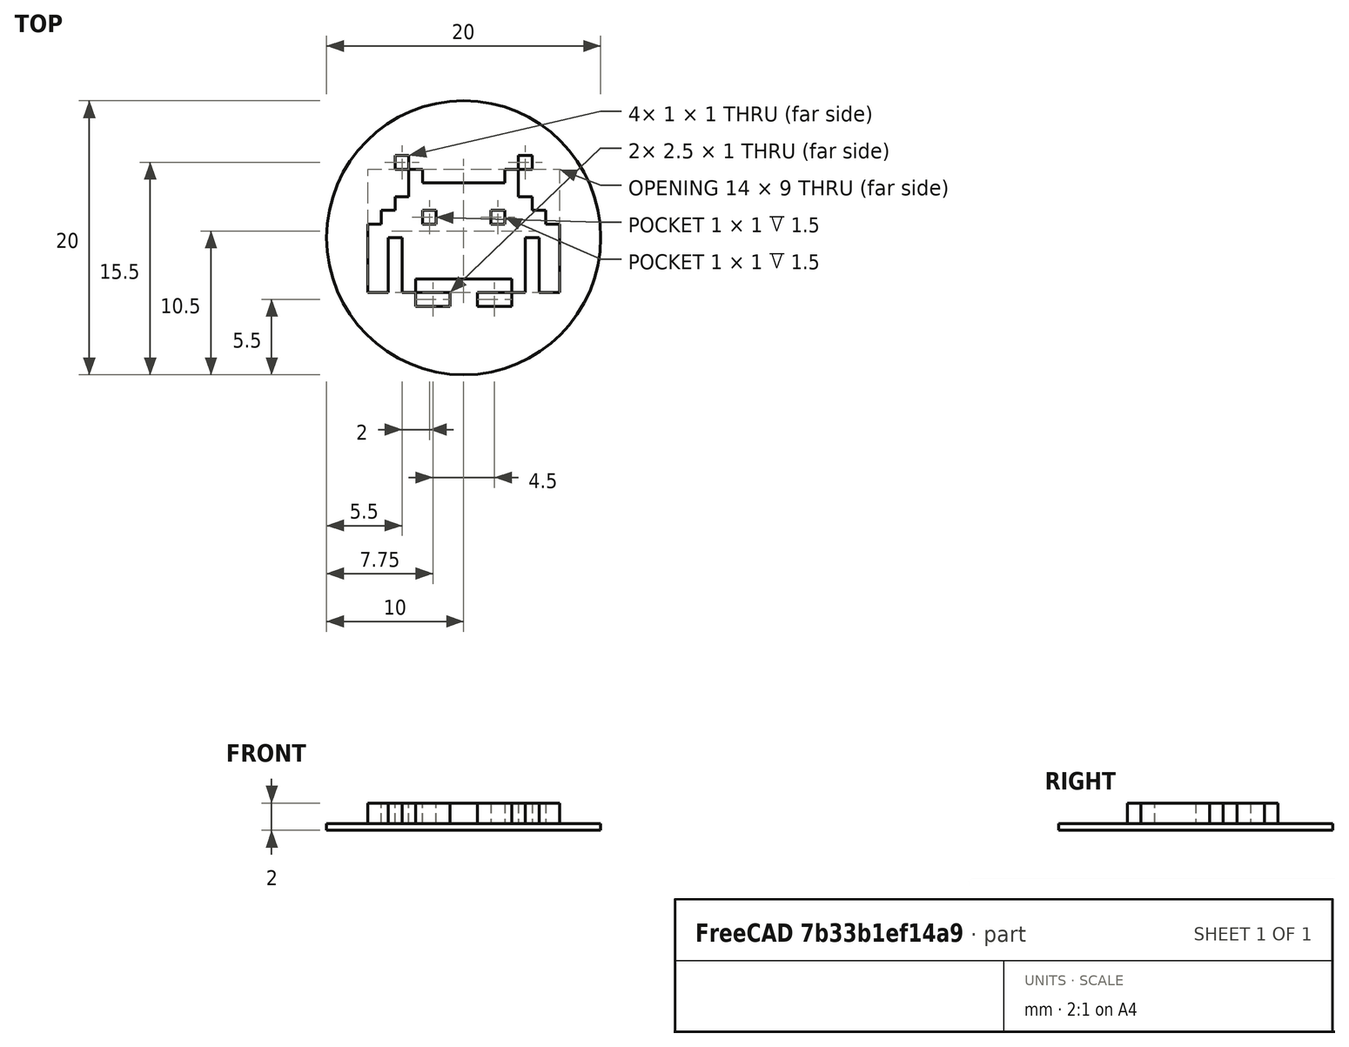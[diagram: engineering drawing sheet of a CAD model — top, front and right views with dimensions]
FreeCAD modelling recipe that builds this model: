
FCSTD DOCUMENT  (FreeCAD 0.20R29177 +233 (Git))
Label: marcianito
License: All rights reserved
LicenseURL: http://en.wikipedia.org/wiki/All_rights_reserved
objects: Part::Box×30, Part::Cut×22, Part::MultiFuse×4, Part::Cylinder×1
note: 57 computed .brp shape members not serialized (recipe doc carries the construction recipe); baked Part::Feature solids carry a one-line shape summary decoded from their .brp

FEATURE [Part::Cylinder] Cylinder  label="Cilindro"
  Angle = 360
  AttacherType = Attacher::AttachEngine3D
  FirstAngle = 0
  Height = 0.5
  Radius = 10
  SecondAngle = 0
FEATURE [Part::Box] Box  label="Cubo"
  AttacherType = Attacher::AttachEngine3D
  Height = 2
  Length = 7
  Placement = pos=(-7,-5,0) rot=(0,0,1;0rad)
  Width = 10
FEATURE [Part::Box] Box001  label="Cubo001"
  AttacherType = Attacher::AttachEngine3D
  Height = 2
  Length = 1
  Placement = pos=(-7,0,0) rot=(0,0,1;0rad)
  Width = 1
FEATURE [Part::Box] Box002  label="Cubo002"
  AttacherType = Attacher::AttachEngine3D
  Height = 2
  Length = 1
  Placement = pos=(-3,0,0) rot=(0,0,1;0rad)
  Width = 1
FEATURE [Part::Box] Box003  label="Cubo003"
  AttacherType = Attacher::AttachEngine3D
  Height = 2
  Length = 1
  Placement = pos=(-5,2,0) rot=(0,0,1;0rad)
  Width = 1
FEATURE [Part::Box] Box004  label="Cubo004"
  AttacherType = Attacher::AttachEngine3D
  Height = 2
  Length = 4
  Placement = pos=(-5.5,-1,0) rot=(0,0,1;4.71239rad)
  Width = 1
FEATURE [Part::Box] Box005  label="Cubo005"
  AttacherType = Attacher::AttachEngine3D
  Height = 2
  Length = 1
  Placement = pos=(-5,4,0) rot=(0,0,1;0rad)
  Width = 1
FEATURE [Part::Box] Box006  label="Cubo006"
  AttacherType = Attacher::AttachEngine3D
  Height = 2
  Length = 1
  Placement = pos=(-6,1,0) rot=(0,0,1;0rad)
  Width = 1
FEATURE [Part::Box] Box007  label="Cubo007"
  AttacherType = Attacher::AttachEngine3D
  Height = 2
  Length = 4
  Placement = pos=(-4,3,0) rot=(0,0,1;0rad)
  Width = 1
FEATURE [Part::Box] Box008  label="Cubo008"
  AttacherType = Attacher::AttachEngine3D
  Height = 2
  Length = 3.5
  Placement = pos=(-3.5,-5,0) rot=(0,0,1;0rad)
  Width = 1
FEATURE [Part::Cut] Cut
  Base = -> Box
  Tool = -> Box001
FEATURE [Part::Cut] Cut001
  Base = -> Cut
  Tool = -> Box008
FEATURE [Part::Cut] Cut002
  Base = -> Cut001
  Tool = -> Box007
FEATURE [Part::Cut] Cut003
  Base = -> Cut002
  Tool = -> Box006
FEATURE [Part::Cut] Cut004
  Base = -> Cut003
  Tool = -> Box005
FEATURE [Part::Cut] Cut005
  Base = -> Cut004
  Tool = -> Box004
FEATURE [Part::Cut] Cut006
  Base = -> Cut005
  Tool = -> Box003
FEATURE [Part::Cut] Cut007
  Base = -> Cut006
  Tool = -> Box002
FEATURE [Part::Box] Box009  label="Cubo009"
  AttacherType = Attacher::AttachEngine3D
  Height = 10
  Length = 10
  Placement = pos=(-4,3,0) rot=(0,0,1;0rad)
  Width = 10
FEATURE [Part::Cut] Cut008
  Base = -> Cut007
  Tool = -> Box009
FEATURE [Part::Box] Box010  label="Cubo010"
  AttacherType = Attacher::AttachEngine3D
  Height = 2
  Length = 1
  Placement = pos=(-5,3,0) rot=(0,0,1;0rad)
  Width = 1
FEATURE [Part::Box] Box011  label="Cubo011"
  AttacherType = Attacher::AttachEngine3D
  Height = 2
  Length = 1
  Placement = pos=(-5,4,0) rot=(0,0,1;0rad)
  Width = 1
FEATURE [Part::Box] Box012  label="Cubo012"
  AttacherType = Attacher::AttachEngine3D
  Height = 10
  Length = 10
  Placement = pos=(-15,1,0) rot=(0,0,1;0rad)
  Width = 10
FEATURE [Part::Cut] Cut009
  Base = -> Cut008
  Tool = -> Box012
FEATURE [Part::Box] Box013  label="Cubo013"
  AttacherType = Attacher::AttachEngine3D
  Height = 2
  Length = 1
  Placement = pos=(-4,3,0) rot=(0,0,1;0rad)
  Width = 1
FEATURE [Part::Cut] Cut010
  Base = -> Cut009
  Tool = -> Box010
FEATURE [Part::Box] Box014  label="Cubo014"
  AttacherType = Attacher::AttachEngine3D
  Height = 2
  Length = 2.5
  Placement = pos=(-3.5,-6,0) rot=(0,0,1;0rad)
  Width = 1
FEATURE [Part::MultiFuse] Fusion
  Shapes = -> [Box014,Cut010,Box013,Box011]
FEATURE [Part::Box] Box015  label="Cubo015"
  AttacherType = Attacher::AttachEngine3D
  Height = 2
  Length = 7
  Placement = pos=(-7,-5,0) rot=(0,0,1;0rad)
  Width = 10
FEATURE [Part::Box] Box016  label="Cubo016"
  AttacherType = Attacher::AttachEngine3D
  Height = 2
  Length = 1
  Placement = pos=(-7,0,0) rot=(0,0,1;0rad)
  Width = 1
FEATURE [Part::Box] Box017  label="Cubo017"
  AttacherType = Attacher::AttachEngine3D
  Height = 2
  Length = 1
  Placement = pos=(-3,0,0) rot=(0,0,1;0rad)
  Width = 1
FEATURE [Part::Box] Box018  label="Cubo018"
  AttacherType = Attacher::AttachEngine3D
  Height = 2
  Length = 1
  Placement = pos=(-5,2,0) rot=(0,0,1;0rad)
  Width = 1
FEATURE [Part::Box] Box019  label="Cubo019"
  AttacherType = Attacher::AttachEngine3D
  Height = 2
  Length = 4
  Placement = pos=(-5.5,-1,0) rot=(0,0,-1;1.5708rad)
  Width = 1
FEATURE [Part::Box] Box020  label="Cubo020"
  AttacherType = Attacher::AttachEngine3D
  Height = 2
  Length = 1
  Placement = pos=(-5,4,0) rot=(0,0,1;0rad)
  Width = 1
FEATURE [Part::Box] Box021  label="Cubo021"
  AttacherType = Attacher::AttachEngine3D
  Height = 2
  Length = 1
  Placement = pos=(-6,1,0) rot=(0,0,1;0rad)
  Width = 1
FEATURE [Part::Box] Box022  label="Cubo022"
  AttacherType = Attacher::AttachEngine3D
  Height = 2
  Length = 4
  Placement = pos=(-4,3,0) rot=(0,0,1;0rad)
  Width = 1
FEATURE [Part::Box] Box023  label="Cubo023"
  AttacherType = Attacher::AttachEngine3D
  Height = 2
  Length = 3.5
  Placement = pos=(-3.5,-5,0) rot=(0,0,1;0rad)
  Width = 1
FEATURE [Part::Box] Box024  label="Cubo024"
  AttacherType = Attacher::AttachEngine3D
  Height = 10
  Length = 10
  Placement = pos=(-4,3,0) rot=(0,0,1;0rad)
  Width = 10
FEATURE [Part::Box] Box025  label="Cubo025"
  AttacherType = Attacher::AttachEngine3D
  Height = 2
  Length = 1
  Placement = pos=(-5,3,0) rot=(0,0,1;0rad)
  Width = 1
FEATURE [Part::Box] Box026  label="Cubo026"
  AttacherType = Attacher::AttachEngine3D
  Height = 2
  Length = 1
  Placement = pos=(-5,4,0) rot=(0,0,1;0rad)
  Width = 1
FEATURE [Part::Box] Box027  label="Cubo027"
  AttacherType = Attacher::AttachEngine3D
  Height = 10
  Length = 10
  Placement = pos=(-15,1,0) rot=(0,0,1;0rad)
  Width = 10
FEATURE [Part::Box] Box028  label="Cubo028"
  AttacherType = Attacher::AttachEngine3D
  Height = 2
  Length = 1
  Placement = pos=(-4,3,0) rot=(0,0,1;0rad)
  Width = 1
FEATURE [Part::Box] Box029  label="Cubo029"
  AttacherType = Attacher::AttachEngine3D
  Height = 2
  Length = 2.5
  Placement = pos=(-3.5,-6,0) rot=(0,0,1;0rad)
  Width = 1
FEATURE [Part::Cut] Cut011
  Base = -> Box015
  Tool = -> Box016
FEATURE [Part::Cut] Cut012
  Base = -> Cut011
  Tool = -> Box023
FEATURE [Part::Cut] Cut013
  Base = -> Cut012
  Tool = -> Box022
FEATURE [Part::Cut] Cut014
  Base = -> Cut013
  Tool = -> Box021
FEATURE [Part::Cut] Cut015
  Base = -> Cut014
  Tool = -> Box020
FEATURE [Part::Cut] Cut016
  Base = -> Cut015
  Tool = -> Box019
FEATURE [Part::Cut] Cut017
  Base = -> Cut016
  Tool = -> Box018
FEATURE [Part::Cut] Cut018
  Base = -> Cut017
  Tool = -> Box017
FEATURE [Part::Cut] Cut019
  Base = -> Cut018
  Tool = -> Box024
FEATURE [Part::Cut] Cut020
  Base = -> Cut019
  Tool = -> Box027
FEATURE [Part::Cut] Cut021
  Base = -> Cut020
  Tool = -> Box025
FEATURE [Part::MultiFuse] Fusion001
  Placement = pos=(-2e-16,0,2) rot=(0,1,0;3.14159rad)
  Shapes = -> [Box029,Cut021,Box028,Box026]
FEATURE [Part::MultiFuse] Fusion002
  Placement = pos=(0,1,0) rot=(0,0,1;0rad)
  Shapes = -> [Fusion,Fusion001]
FEATURE [Part::MultiFuse] Fusion003
  Shapes = -> [Cylinder,Fusion002]
